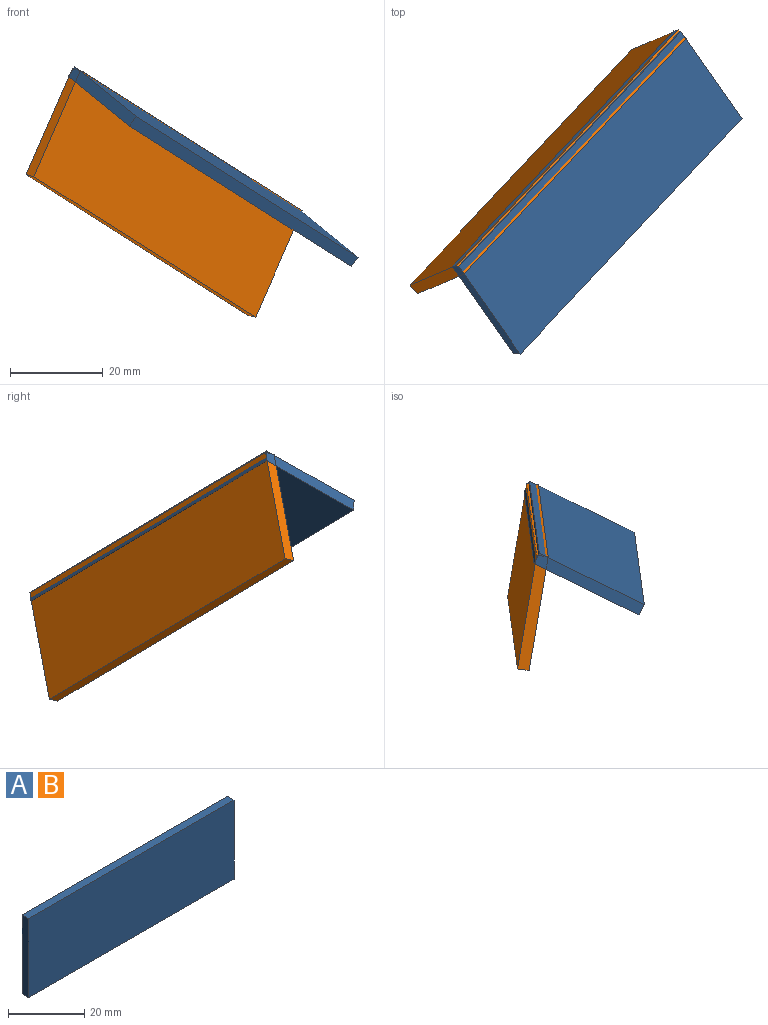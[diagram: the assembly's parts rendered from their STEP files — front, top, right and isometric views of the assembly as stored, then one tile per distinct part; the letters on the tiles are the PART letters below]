
ASSEMBLY  parts=2 mates=1
PART A: 11 faces, bbox 76.2x2.5x25.4 mm
  f0: plane 25.4x2.54mm, normal (-1,0,0), area 64.5mm2, adj f1,f3,f4,f5
  f1: plane 76.2x2.54mm, normal (0,0,-1), area 193.5mm2, adj f0,f2,f4,f5
  f2: plane 25.4x2.54mm, normal (1,0,0), area 62.9mm2, adj f1,f3,f4,f5,f6,f7,f8,f9
  f3: plane 76.2x2.54mm, normal (0,0,1), area 193.5mm2, adj f0,f2,f4,f5
  f4: plane 76.2x25.4mm, normal (0,-1,0), area 1935.5mm2, adj f0,f1,f2,f3
  f5: plane 76.2x25.4mm, normal (0,1,0), area 1935.5mm2, adj f0,f1,f2,f3
  f6: plane 1.27x0.03mm, normal (0,1,0), area 0mm2, adj f2,f7,f9,f10
  f7: plane 1.27x0.03mm, normal (0,0,1), area 0mm2, adj f2,f6,f8,f10
  f8: plane 1.27x0.03mm, normal (0,-1,0), area 0mm2, adj f2,f7,f9,f10
  f9: plane 1.27x0.03mm, normal (0,0,-1), area 0mm2, adj f2,f6,f8,f10
  f10: plane 1.27x1.27mm, normal (1,0,0), area 1.6mm2, adj f6,f7,f8,f9
PART B: same geometry as A
PLACE A rot(axis=(-0.78,-0.06,0.62),86.9deg) t=(19.48,-35.18,20.88)mm
PLACE B rot(axis=(0,0.51,0.86),51deg) t=(8.78,-27.72,16.49)mm
MATE revolute B.f10 <-> A.f10  axis (0.63,0.67,-0.4) through (38.13,-1.2,11.56)mm
